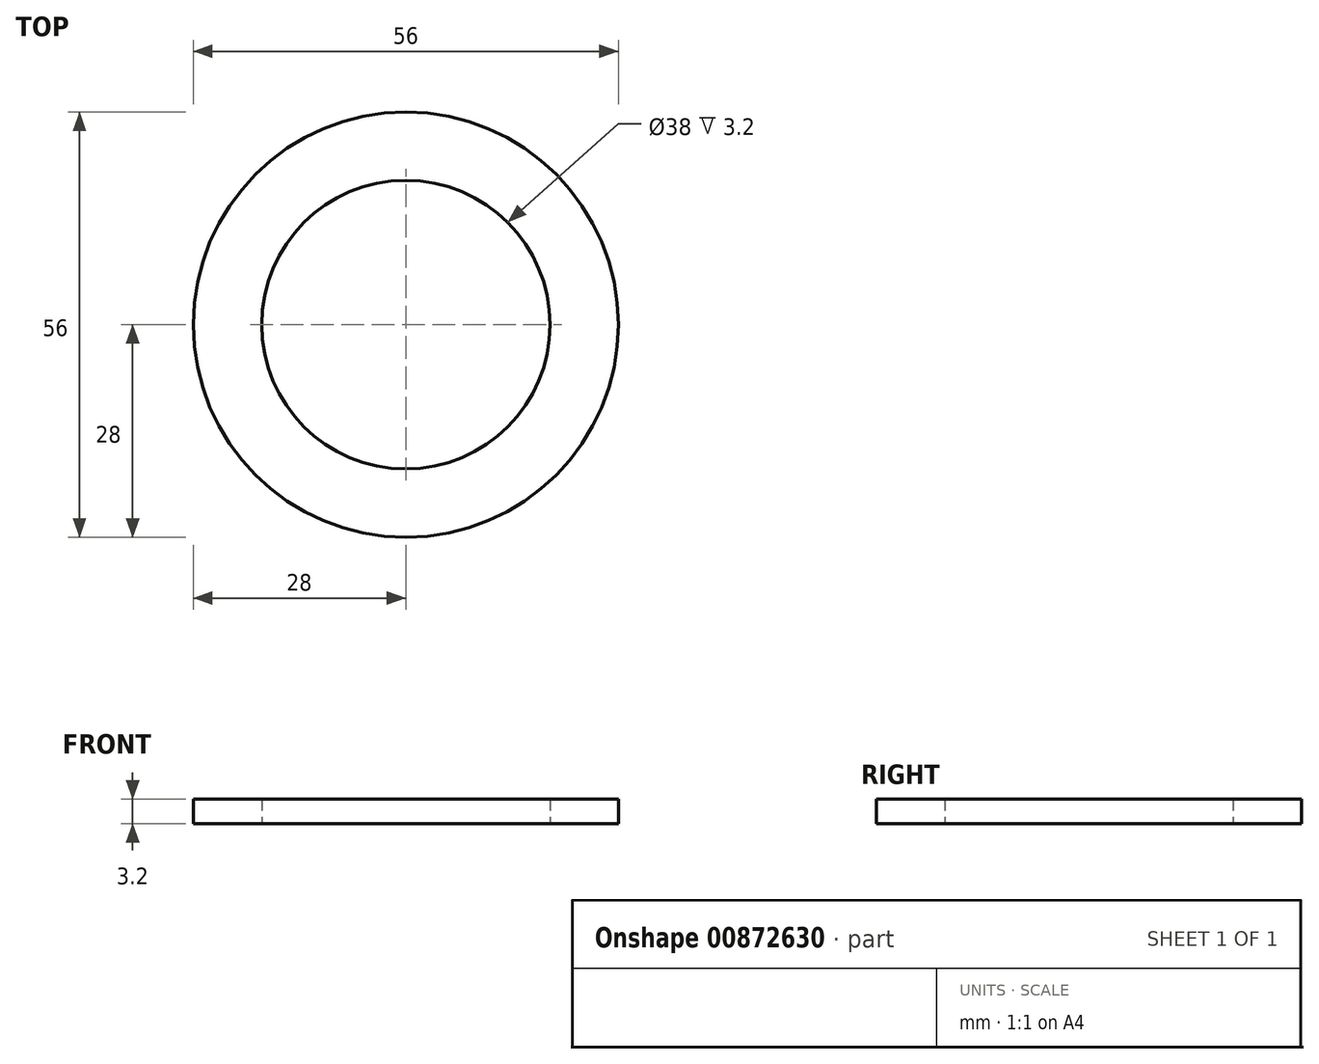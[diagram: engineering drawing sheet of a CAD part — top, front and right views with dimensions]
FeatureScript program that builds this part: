
annotation { "Feature Type Name" : "Feature", "Feature Type Description" : "" }
export const myFeature = defineFeature(function(context is Context, id is Id, definition is map)
    precondition{}
    {
        {
            var Q0;
            Q0=qCreatedBy(makeId("Top.planeOp"),FACE);
            var sketch = newSketch(context, id + "F0", { "sketchPlane" : qUnion([Q0])});
            skCircle(sketch, "E0", {"center": v(0, 0) * mm, "radius": 28 * mm});
            skCircle(sketch, "E1", {"center": v(0, 0) * mm, "radius": 19 * mm});
            skSolve(sketch);
        }
        {
            var Q0;
            Q0 = qSketchRegion(id + "F0", true);
            extrude(context, id + "F1", {"entities" : qUnion([Q0]), "depth" : 3.2 * mm, "offsetDistance" : 25 * mm});
        }
    });
